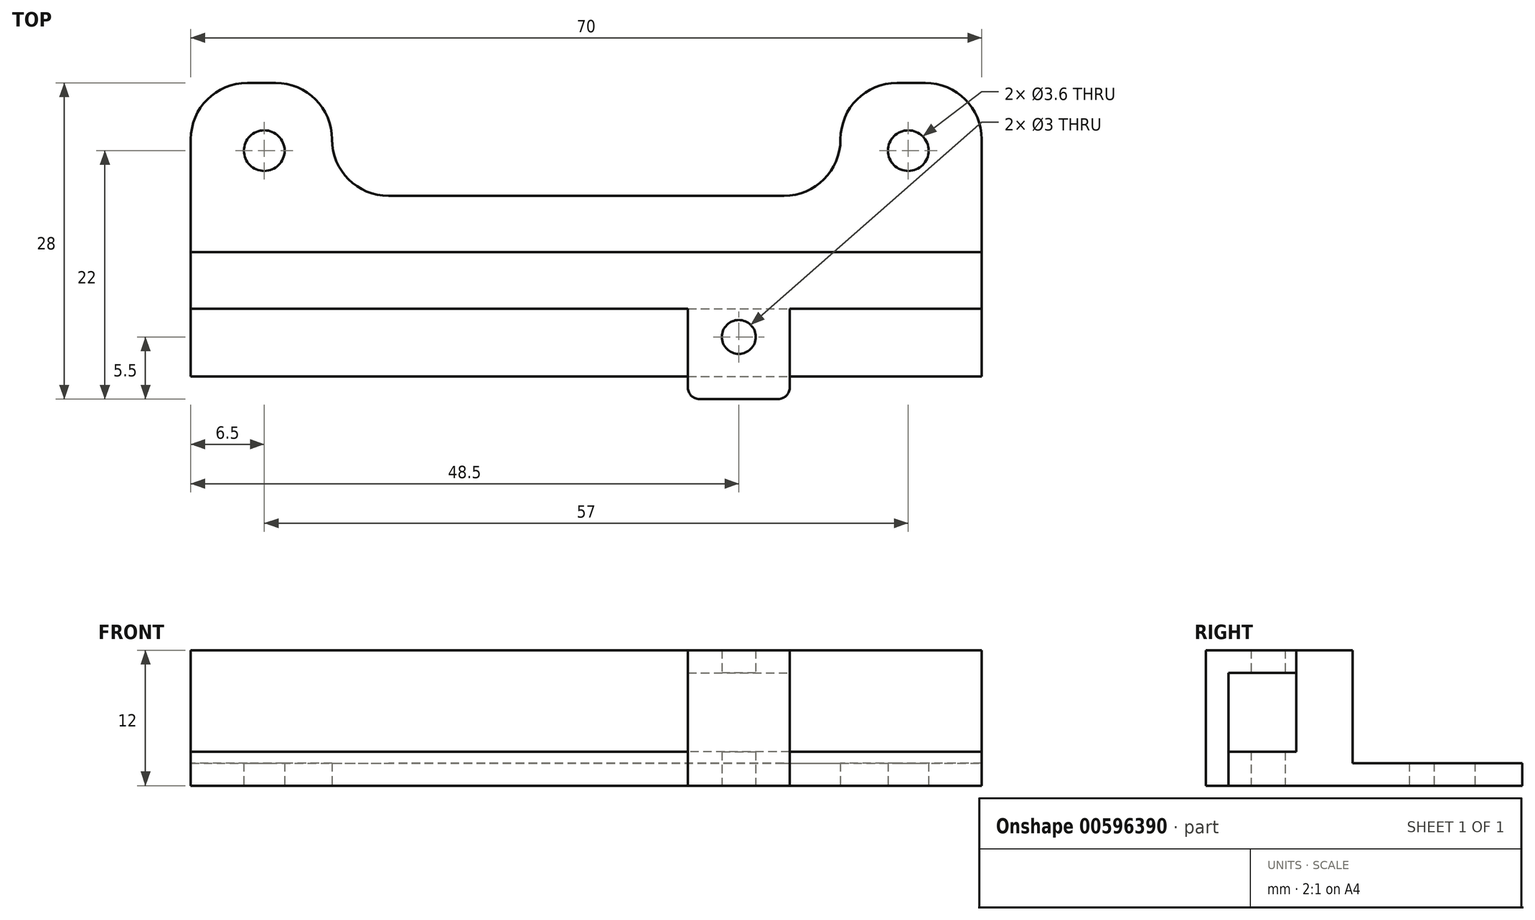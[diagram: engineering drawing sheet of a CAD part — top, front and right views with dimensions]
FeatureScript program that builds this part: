
annotation { "Feature Type Name" : "Feature", "Feature Type Description" : "" }
export const myFeature = defineFeature(function(context is Context, id is Id, definition is map)
    precondition{}
    {
        {
            var Q0;
            Q0=qCreatedBy(makeId("Top.planeOp"),FACE);
            var sketch = newSketch(context, id + "F0", { "sketchPlane" : qUnion([Q0])});
            skLineSegment(sketch, "E0.bottom", {"start": v(-35, 10) * mm, "end": v(-22.5, 10) * mm});
            skLineSegment(sketch, "E0.top", {"start": v(-35, -10) * mm, "end": v(35, -10) * mm});
            skLineSegment(sketch, "E0.left", {"start": v(-35, 10) * mm, "end": v(-35, -10) * mm});
            skLineSegment(sketch, "E0.right", {"start": v(35, 10) * mm, "end": v(35, -10) * mm});
            skCircle(sketch, "E1", {"center": v(-28.5, 4) * mm, "radius": 1.8 * mm});
            skLineSegment(sketch, "E2", {"start": v(0, 0) * mm, "end": v(0, 14.4) * mm, "construction": true});
            skLineSegment(sketch, "E3", {"start": v(-22.5, 10) * mm, "end": v(-22.5, 0) * mm});
            skLineSegment(sketch, "E4", {"start": v(-22.5, 0) * mm, "end": v(0, 0) * mm});
            skLineSegment(sketch, "E5.MirrorCS", {"start": v(22.5, 10) * mm, "end": v(22.5, 0) * mm});
            skLineSegment(sketch, "E6.MirrorCS", {"start": v(22.5, 0) * mm, "end": v(0, 0) * mm});
            skCircle(sketch, "E7.MirrorC", {"center": v(28.5, 4) * mm, "radius": 1.8 * mm});
            skLineSegment(sketch, "E8.trimOffspring", {"start": v(22.5, 10) * mm, "end": v(35, 10) * mm});
            skSolve(sketch);
        }
        {
            var Q0;
            Q0=makeQuery(id+"F0.imprint","IMPRINT",FACE,{"disambiguationData":[TD([[makeQuery(id+"F0.imprint","IMPRINT",EDGE,{"derivedFrom":sQuery(id+"F0.wireOp",EDGE,"E0.bottom")}),-1.0]])]});
            extrude(context, id + "F1", {"entities" : qUnion([Q0]), "depth" : 2 * mm, "offsetDistance" : 25 * mm});
        }
        {
            var Q0;
            Q0=makeQuery(id+"F1.opExtrude","SWEPT_EDGE",EDGE,{"disambiguationData":[OSD([sQuery(id+"F0.wireOp",EDGE,"E5.MirrorCS"),sQuery(id+"F0.wireOp",EDGE,"E8.trimOffspring")])]});
            var Q1;
            Q1=makeQuery(id+"F1.opExtrude","SWEPT_EDGE",EDGE,{"disambiguationData":[OSD([sQuery(id+"F0.wireOp",EDGE,"E0.right"),sQuery(id+"F0.wireOp",EDGE,"E8.trimOffspring")])]});
            var Q2;
            Q2=makeQuery(id+"F1.opExtrude","SWEPT_EDGE",EDGE,{"disambiguationData":[OSD([sQuery(id+"F0.wireOp",EDGE,"E0.bottom"),sQuery(id+"F0.wireOp",EDGE,"E3")])]});
            var Q3;
            Q3=makeQuery(id+"F1.opExtrude","SWEPT_EDGE",EDGE,{"disambiguationData":[OSD([sQuery(id+"F0.wireOp",EDGE,"E0.bottom"),sQuery(id+"F0.wireOp",EDGE,"E0.left")])]});
            var Q4;
            Q4=makeQuery(id+"F1.opExtrude","SWEPT_EDGE",EDGE,{"disambiguationData":[OSD([sQuery(id+"F0.wireOp",EDGE,"E3"),sQuery(id+"F0.wireOp",EDGE,"E4")])]});
            var Q5;
            Q5=makeQuery(id+"F1.opExtrude","SWEPT_EDGE",EDGE,{"disambiguationData":[OSD([sQuery(id+"F0.wireOp",EDGE,"E5.MirrorCS"),sQuery(id+"F0.wireOp",EDGE,"E6.MirrorCS")])]});
            fillet(context, id + "F2", {"entities" : qUnion([Q0, Q1, Q2, Q3, Q4, Q5]), "radius" : 5 * mm, "tangentPropagation" : true, "allowEdgeOverflow" : false});
        }
        {
            var Q0;
            Q0=makeQuery(id+"F1.opExtrude","CAP_FACE",FACE,{"disambiguationData":[OSD([sQuery(id+"F0.wireOp",EDGE,"E0.bottom"),sQuery(id+"F0.wireOp",EDGE,"E0.top"),sQuery(id+"F0.wireOp",EDGE,"E0.left"),sQuery(id+"F0.wireOp",EDGE,"E0.right"),sQuery(id+"F0.wireOp",EDGE,"E1"),sQuery(id+"F0.wireOp",EDGE,"E3"),sQuery(id+"F0.wireOp",EDGE,"E4"),sQuery(id+"F0.wireOp",EDGE,"E5.MirrorCS"),sQuery(id+"F0.wireOp",EDGE,"E6.MirrorCS"),sQuery(id+"F0.wireOp",EDGE,"E7.MirrorC"),sQuery(id+"F0.wireOp",EDGE,"E8.trimOffspring")])],"isStart":false});
            var sketch = newSketch(context, id + "F3", { "sketchPlane" : qUnion([Q0])});
            skLineSegment(sketch, "E9.bottom", {"start": v(-35, -5) * mm, "end": v(35, -5) * mm});
            skLineSegment(sketch, "E9.top", {"start": v(-35, -10) * mm, "end": v(35, -10) * mm});
            skLineSegment(sketch, "E9.left", {"start": v(-35, -5) * mm, "end": v(-35, -10) * mm});
            skLineSegment(sketch, "E9.right", {"start": v(35, -5) * mm, "end": v(35, -10) * mm});
            skSolve(sketch);
        }
        {
            var Q0;
            Q0=makeQuery(id+"F3.imprint","IMPRINT",FACE,{"disambiguationData":[TD([[makeQuery(id+"F3.imprint","IMPRINT",EDGE,{"derivedFrom":sQuery(id+"F3.wireOp",EDGE,"E9.bottom")}),-1.0]])]});
            extrude(context, id + "F4", {"entities" : qUnion([Q0]), "operationType" : NewBodyOperationType.ADD, "depth" : 10 * mm, "offsetDistance" : 25 * mm});
        }
        {
            var Q0;
            Q0=makeQuery(id+"F4.boolean.opBoolean","MERGE",FACE,{"derivedFrom":[makeQuery(id+"F1.opExtrude","SWEPT_FACE",FACE,{"disambiguationData":[OSD([sQuery(id+"F0.wireOp",EDGE,"E0.top")])]}),makeQuery(id+"F4.opExtrude","SWEPT_FACE",FACE,{"disambiguationData":[OSD([sQuery(id+"F3.wireOp",EDGE,"E9.top")])]})]});
            var sketch = newSketch(context, id + "F5", { "sketchPlane" : qUnion([Q0])});
            skLineSegment(sketch, "E10.bottom", {"start": v(35, 0) * mm, "end": v(-35, 0) * mm});
            skLineSegment(sketch, "E10.top", {"start": v(35, 3) * mm, "end": v(-35, 3) * mm});
            skLineSegment(sketch, "E10.left", {"start": v(35, 0) * mm, "end": v(35, 3) * mm});
            skLineSegment(sketch, "E10.right", {"start": v(-35, 0) * mm, "end": v(-35, 3) * mm});
            skSolve(sketch);
        }
        {
            var Q0;
            Q0=makeQuery(id+"F5.imprint","IMPRINT",FACE,{"disambiguationData":[TD([[makeQuery(id+"F5.imprint","IMPRINT",EDGE,{"derivedFrom":sQuery(id+"F5.wireOp",EDGE,"E10.bottom")}),1.0]])]});
            extrude(context, id + "F6", {"entities" : qUnion([Q0]), "operationType" : NewBodyOperationType.ADD, "depth" : 6 * mm, "offsetDistance" : 25 * mm});
        }
        {
            var Q0;
            Q0=makeQuery(id+"F6.boolean.opBoolean","MERGE",FACE,{"derivedFrom":[makeQuery(id+"F1.opExtrude","CAP_FACE",FACE,{"disambiguationData":[OSD([sQuery(id+"F0.wireOp",EDGE,"E0.bottom"),sQuery(id+"F0.wireOp",EDGE,"E0.top"),sQuery(id+"F0.wireOp",EDGE,"E0.left"),sQuery(id+"F0.wireOp",EDGE,"E0.right"),sQuery(id+"F0.wireOp",EDGE,"E1"),sQuery(id+"F0.wireOp",EDGE,"E3"),sQuery(id+"F0.wireOp",EDGE,"E4"),sQuery(id+"F0.wireOp",EDGE,"E5.MirrorCS"),sQuery(id+"F0.wireOp",EDGE,"E6.MirrorCS"),sQuery(id+"F0.wireOp",EDGE,"E7.MirrorC"),sQuery(id+"F0.wireOp",EDGE,"E8.trimOffspring")])],"isStart":true}),makeQuery(id+"F6.opExtrude","SWEPT_FACE",FACE,{"disambiguationData":[OSD([sQuery(id+"F5.wireOp",EDGE,"E10.bottom")])]})]});
            var sketch = newSketch(context, id + "F7", { "sketchPlane" : qUnion([Q0])});
            skCircle(sketch, "E11", {"center": v(13.5, 12.5) * mm, "radius": 1.5 * mm});
            skSolve(sketch);
        }
        {
            var Q0;
            Q0=makeQuery(id+"F4.boolean.opBoolean","MERGE",FACE,{"derivedFrom":[makeQuery(id+"F1.opExtrude","SWEPT_FACE",FACE,{"disambiguationData":[OSD([sQuery(id+"F0.wireOp",EDGE,"E0.top")])]}),makeQuery(id+"F4.opExtrude","SWEPT_FACE",FACE,{"disambiguationData":[OSD([sQuery(id+"F3.wireOp",EDGE,"E9.top")])]})]});
            var sketch = newSketch(context, id + "F8", { "sketchPlane" : qUnion([Q0])});
            skLineSegment(sketch, "E12.bottom", {"start": v(9, 12) * mm, "end": v(18, 12) * mm});
            skLineSegment(sketch, "E12.top", {"start": v(9, 10) * mm, "end": v(18, 10) * mm});
            skLineSegment(sketch, "E12.left", {"start": v(9, 12) * mm, "end": v(9, 10) * mm});
            skLineSegment(sketch, "E12.right", {"start": v(18, 12) * mm, "end": v(18, 10) * mm});
            skSolve(sketch);
        }
        {
            var Q0;
            Q0=makeQuery(id+"F8.imprint","IMPRINT",FACE,{"disambiguationData":[TD([[makeQuery(id+"F8.imprint","IMPRINT",EDGE,{"derivedFrom":sQuery(id+"F8.wireOp",EDGE,"E12.bottom")}),-1.0]])]});
            extrude(context, id + "F9", {"entities" : qUnion([Q0]), "operationType" : NewBodyOperationType.ADD, "depth" : 8 * mm, "offsetDistance" : 25 * mm});
        }
        {
            var Q0;
            Q0=makeQuery(id+"F9.opExtrude","SWEPT_FACE",FACE,{"disambiguationData":[OSD([sQuery(id+"F8.wireOp",EDGE,"E12.top")])]});
            var sketch = newSketch(context, id + "F10", { "sketchPlane" : qUnion([Q0])});
            skLineSegment(sketch, "E13.bottom", {"start": v(9, 18) * mm, "end": v(18, 18) * mm});
            skLineSegment(sketch, "E13.top", {"start": v(9, 16) * mm, "end": v(18, 16) * mm});
            skLineSegment(sketch, "E13.left", {"start": v(9, 18) * mm, "end": v(9, 16) * mm});
            skLineSegment(sketch, "E13.right", {"start": v(18, 18) * mm, "end": v(18, 16) * mm});
            skSolve(sketch);
        }
        {
            var Q0;
            Q0=makeQuery(id+"F10.imprint","IMPRINT",FACE,{"disambiguationData":[TD([[makeQuery(id+"F10.imprint","IMPRINT",EDGE,{"derivedFrom":sQuery(id+"F10.wireOp",EDGE,"E13.bottom")}),-1.0]])]});
            extrude(context, id + "F11", {"entities" : qUnion([Q0]), "operationType" : NewBodyOperationType.ADD, "depth" : 10 * mm, "offsetDistance" : 25 * mm});
        }
        {
            var Q0;
            Q0=makeQuery(id+"F7.imprint","IMPRINT",FACE,{"disambiguationData":[TD([[makeQuery(id+"F7.imprint","IMPRINT",EDGE,{"derivedFrom":sQuery(id+"F7.wireOp",EDGE,"E11")}),1.0]])]});
            extrude(context, id + "F12", {"entities" : qUnion([Q0]), "operationType" : NewBodyOperationType.REMOVE, "endBound" : BoundingType.THROUGH_ALL, "oppositeDirection" : true, "depth" : 10 * mm, "offsetDistance" : 25 * mm});
        }
        {
            var Q0;
            Q0=makeQuery(id+"F11.boolean.opBoolean","MERGE",EDGE,{"derivedFrom":[makeQuery(id+"F9.opExtrude","CAP_EDGE",EDGE,{"disambiguationData":[OSD([sQuery(id+"F8.wireOp",EDGE,"E12.left")])],"isStart":false}),makeQuery(id+"F11.opExtrude","SWEPT_EDGE",EDGE,{"disambiguationData":[OSD([sQuery(id+"F10.wireOp",EDGE,"E13.bottom"),sQuery(id+"F10.wireOp",EDGE,"E13.left")])]})]});
            var Q1;
            Q1=makeQuery(id+"F11.boolean.opBoolean","MERGE",EDGE,{"derivedFrom":[makeQuery(id+"F9.opExtrude","CAP_EDGE",EDGE,{"disambiguationData":[OSD([sQuery(id+"F8.wireOp",EDGE,"E12.right")])],"isStart":false}),makeQuery(id+"F11.opExtrude","SWEPT_EDGE",EDGE,{"disambiguationData":[OSD([sQuery(id+"F10.wireOp",EDGE,"E13.bottom"),sQuery(id+"F10.wireOp",EDGE,"E13.right")])]})]});
            fillet(context, id + "F13", {"entities" : qUnion([Q0, Q1]), "radius" : 1 * mm, "tangentPropagation" : true, "allowEdgeOverflow" : false});
        }
    });
